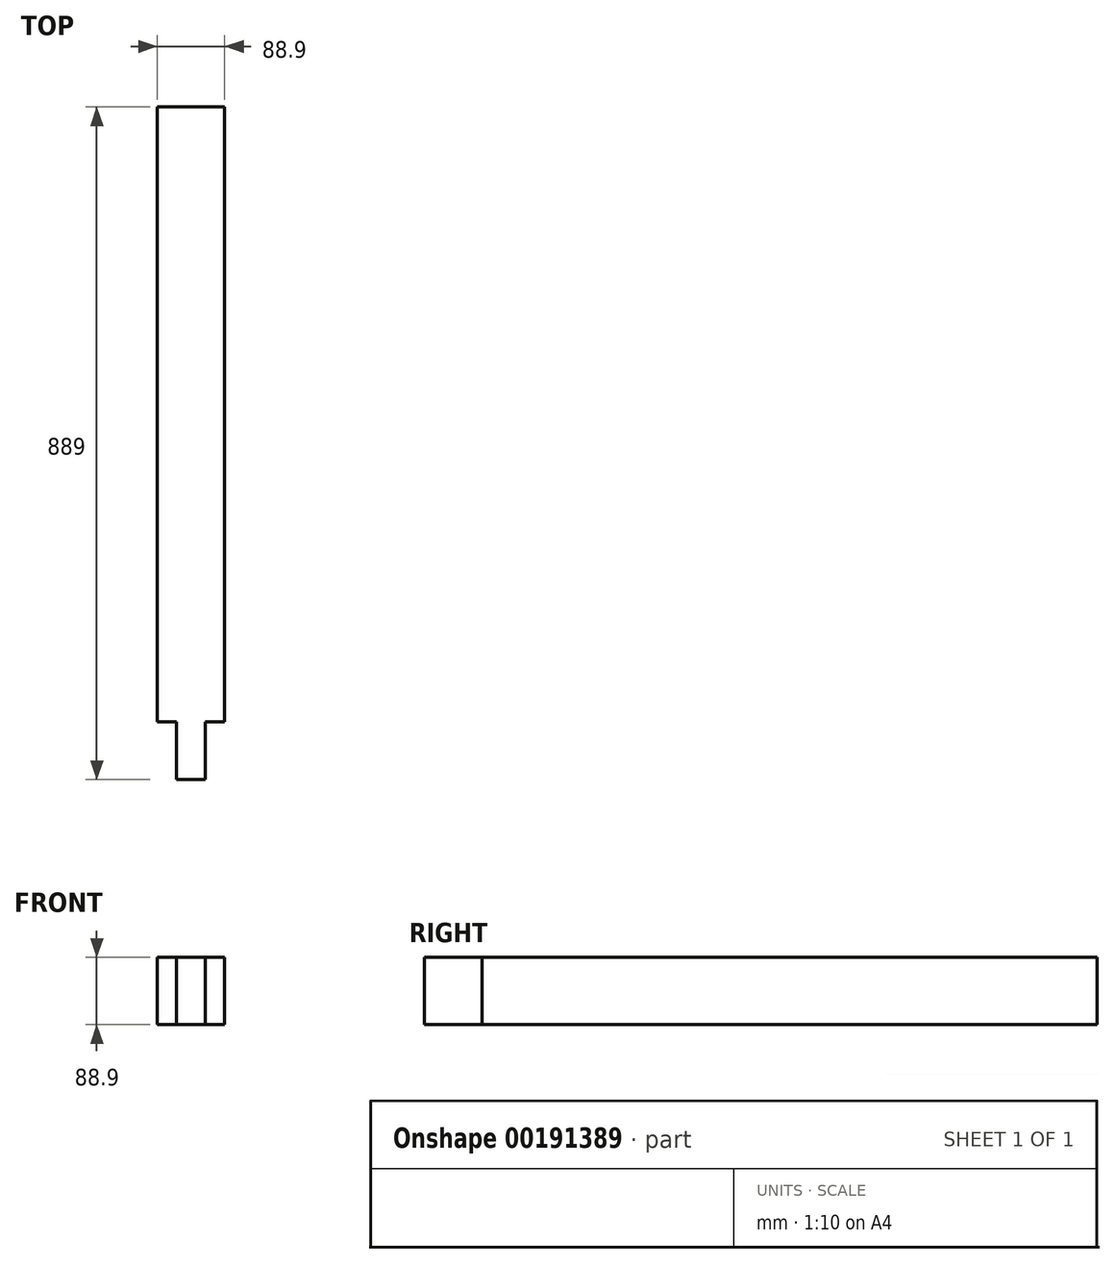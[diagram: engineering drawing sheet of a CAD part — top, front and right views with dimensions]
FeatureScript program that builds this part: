
annotation { "Feature Type Name" : "Feature", "Feature Type Description" : "" }
export const myFeature = defineFeature(function(context is Context, id is Id, definition is map)
    precondition{}
    {
        {
            var Q0;
            Q0=qCreatedBy(makeId("Front.planeOp"),FACE);
            var sketch = newSketch(context, id + "F0", { "sketchPlane" : qUnion([Q0])});
            skLineSegment(sketch, "E0.bottom", {"start": v(-69.5, 84.3) * mm, "end": v(19.4, 84.3) * mm});
            skLineSegment(sketch, "E0.top", {"start": v(-69.5, -4.6) * mm, "end": v(19.4, -4.6) * mm});
            skLineSegment(sketch, "E0.left", {"start": v(-69.5, 84.3) * mm, "end": v(-69.5, -4.6) * mm});
            skLineSegment(sketch, "E0.right", {"start": v(19.4, 84.3) * mm, "end": v(19.4, -4.6) * mm});
            skSolve(sketch);
        }
        {
            var Q0;
            Q0=makeQuery(id+"F0.imprint","IMPRINT",FACE,{"disambiguationData":[TD([[makeQuery(id+"F0.imprint","IMPRINT",EDGE,{"derivedFrom":sQuery(id+"F0.wireOp",EDGE,"E0.bottom")}),-1.0]])]});
            extrude(context, id + "F1", {"entities" : qUnion([Q0]), "depth" : 889 * mm});
        }
        {
            var Q0;
            Q0=makeQuery(id+"F1.opExtrude","SWEPT_FACE",FACE,{"disambiguationData":[OSD([sQuery(id+"F0.wireOp",EDGE,"E0.bottom")])]});
            var sketch = newSketch(context, id + "F2", { "sketchPlane" : qUnion([Q0])});
            skLineSegment(sketch, "E1.bottom", {"start": v(19.4, -889) * mm, "end": v(-6, -889) * mm});
            skLineSegment(sketch, "E1.top", {"start": v(19.4, -812.8) * mm, "end": v(-6, -812.8) * mm});
            skLineSegment(sketch, "E1.left", {"start": v(19.4, -889) * mm, "end": v(19.4, -812.8) * mm});
            skLineSegment(sketch, "E1.right", {"start": v(-6, -889) * mm, "end": v(-6, -812.8) * mm});
            skLineSegment(sketch, "E2.bottom", {"start": v(-69.5, -889) * mm, "end": v(-44.1, -889) * mm});
            skLineSegment(sketch, "E2.top", {"start": v(-69.5, -812.8) * mm, "end": v(-44.1, -812.8) * mm});
            skLineSegment(sketch, "E2.left", {"start": v(-69.5, -889) * mm, "end": v(-69.5, -812.8) * mm});
            skLineSegment(sketch, "E2.right", {"start": v(-44.1, -889) * mm, "end": v(-44.1, -812.8) * mm});
            skSolve(sketch);
        }
        {
            var Q0;
            Q0 = qSketchRegion(id + "F2", true);
            var Q1;
            Q1 = qConstructionFilter(qBodyType(qCreatedBy(id + "F2" ,EDGE), BodyType.WIRE), ConstructionObject.NO);
            extrude(context, id + "F3", {"entities" : qUnion([Q0]), "operationType" : NewBodyOperationType.REMOVE, "surfaceEntities" : qUnion([Q1]), "endBound" : BoundingType.UP_TO_NEXT, "oppositeDirection" : true, "depth" : 25.4 * mm});
        }
    });
